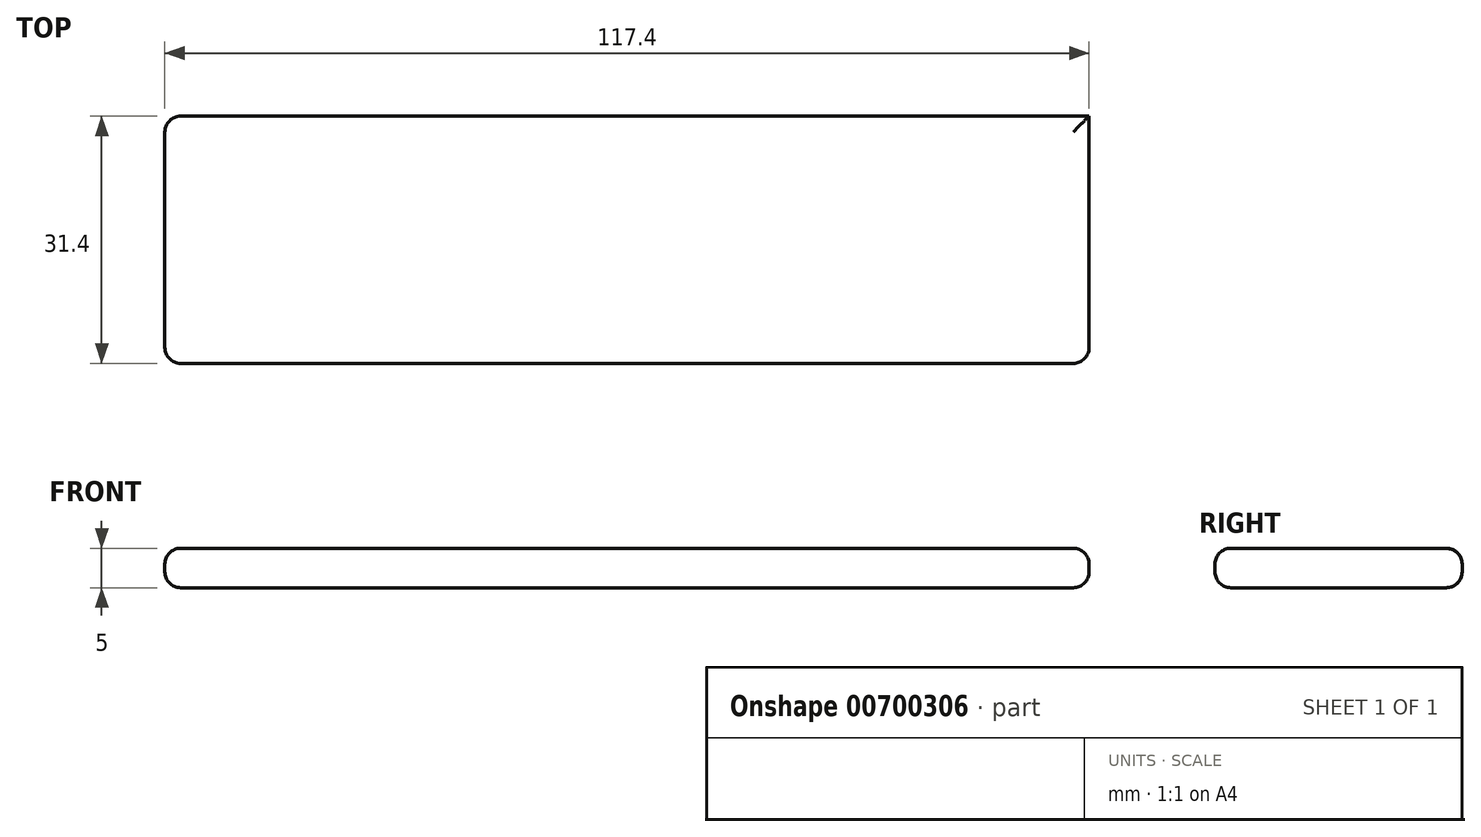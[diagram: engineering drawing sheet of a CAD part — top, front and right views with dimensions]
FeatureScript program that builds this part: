
annotation { "Feature Type Name" : "Feature", "Feature Type Description" : "" }
export const myFeature = defineFeature(function(context is Context, id is Id, definition is map)
    precondition{}
    {
        {
            var Q0;
            Q0=qCreatedBy(makeId("Top.planeOp"),FACE);
            var sketch = newSketch(context, id + "F0", { "sketchPlane" : qUnion([Q0])});
            skLineSegment(sketch, "E0.bottom", {"start": v(58.7, -15.7) * mm, "end": v(-58.7, -15.7) * mm});
            skLineSegment(sketch, "E0.top", {"start": v(58.7, 15.7) * mm, "end": v(-58.7, 15.7) * mm});
            skLineSegment(sketch, "E0.left", {"start": v(58.7, -15.7) * mm, "end": v(58.7, 15.7) * mm});
            skLineSegment(sketch, "E0.right", {"start": v(-58.7, -15.7) * mm, "end": v(-58.7, 15.7) * mm});
            skPoint(sketch, "E0.middle", {"position": v(0, 0) * mm});
            skSolve(sketch);
        }
        {
            var Q0;
            Q0 = qSketchRegion(id + "F0", true);
            extrude(context, id + "F1", {"entities" : qUnion([Q0]), "depth" : 5 * mm, "offsetDistance" : 25 * mm});
        }
        {
            var Q0;
            Q0=makeQuery(id+"F1.opExtrude","CAP_EDGE",EDGE,{"disambiguationData":[OSD([sQuery(id+"F0.wireOp",EDGE,"E0.bottom")])],"isStart":false});
            fillet(context, id + "F2", {"entities" : qUnion([Q0]), "radius" : 2 * mm, "tangentPropagation" : true, "allowEdgeOverflow" : false});
        }
        {
            var Q0;
            Q0=makeQuery(id+"F1.opExtrude","CAP_EDGE",EDGE,{"disambiguationData":[OSD([sQuery(id+"F0.wireOp",EDGE,"E0.left")])],"isStart":false});
            var Q1;
            Q1=makeQuery(id+"F1.opExtrude","CAP_EDGE",EDGE,{"disambiguationData":[OSD([sQuery(id+"F0.wireOp",EDGE,"E0.top")])],"isStart":false});
            fillet(context, id + "F3", {"entities" : qUnion([Q0, Q1]), "radius" : 2 * mm, "tangentPropagation" : true, "allowEdgeOverflow" : false});
        }
        {
            var Q0;
            Q0=makeQuery(id+"F1.opExtrude","CAP_EDGE",EDGE,{"disambiguationData":[OSD([sQuery(id+"F0.wireOp",EDGE,"E0.right")])],"isStart":false});
            fillet(context, id + "F4", {"entities" : qUnion([Q0]), "radius" : 2 * mm, "tangentPropagation" : true, "allowEdgeOverflow" : false});
        }
        {
            var Q0;
            Q0=makeQuery(id+"F1.opExtrude","CAP_EDGE",EDGE,{"disambiguationData":[OSD([sQuery(id+"F0.wireOp",EDGE,"E0.right")])],"isStart":true});
            var Q1;
            Q1=makeQuery(id+"F1.opExtrude","CAP_EDGE",EDGE,{"disambiguationData":[OSD([sQuery(id+"F0.wireOp",EDGE,"E0.bottom")])],"isStart":true});
            var Q2;
            Q2=makeQuery(id+"F1.opExtrude","CAP_EDGE",EDGE,{"disambiguationData":[OSD([sQuery(id+"F0.wireOp",EDGE,"E0.top")])],"isStart":true});
            var Q3;
            Q3=makeQuery(id+"F1.opExtrude","CAP_EDGE",EDGE,{"disambiguationData":[OSD([sQuery(id+"F0.wireOp",EDGE,"E0.left")])],"isStart":true});
            fillet(context, id + "F5", {"entities" : qUnion([Q0, Q1, Q2, Q3]), "radius" : 2 * mm, "tangentPropagation" : true, "allowEdgeOverflow" : false});
        }
    });
